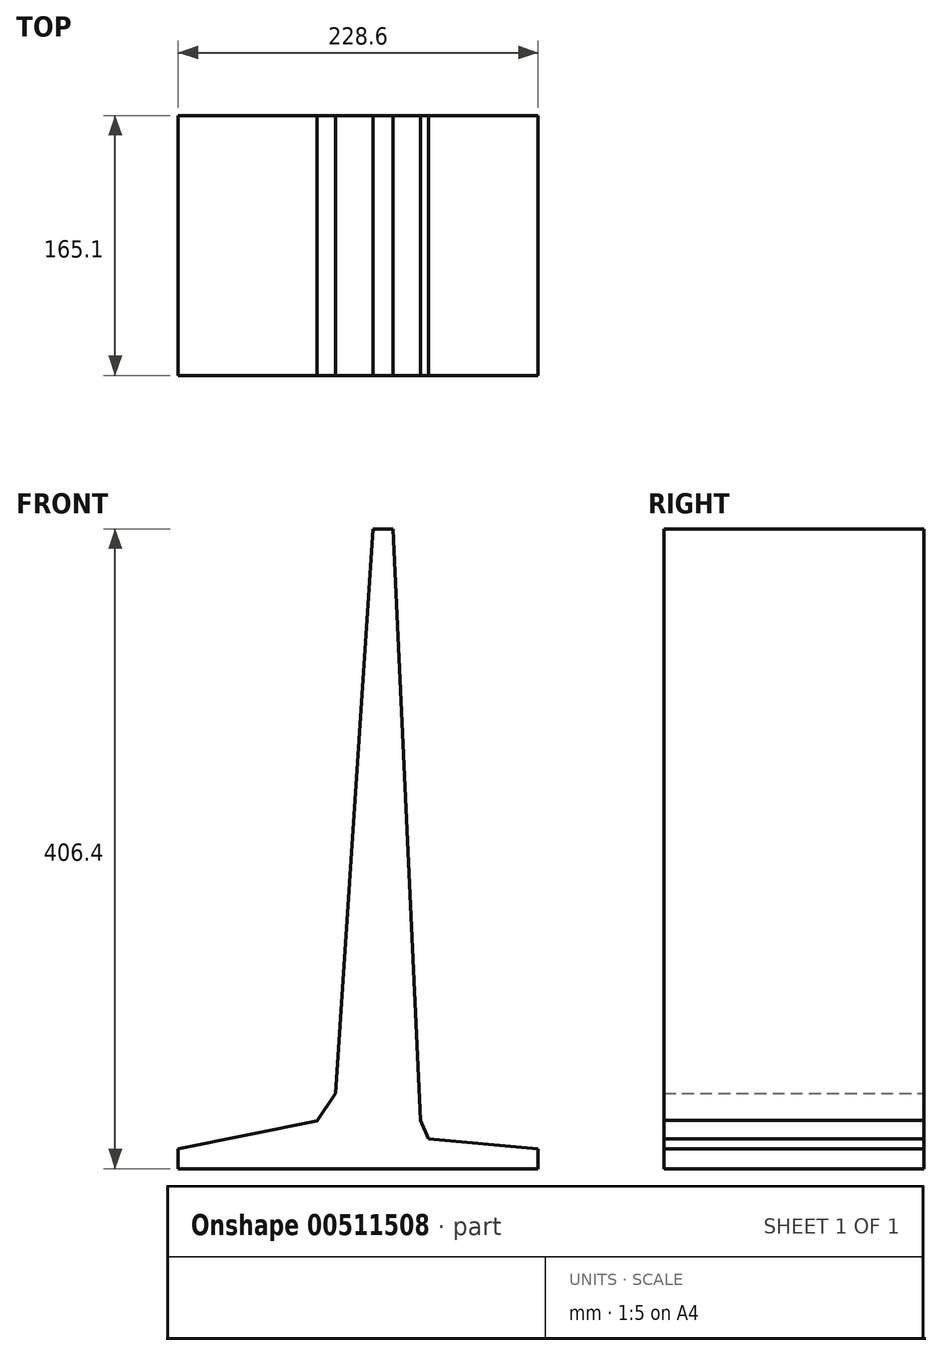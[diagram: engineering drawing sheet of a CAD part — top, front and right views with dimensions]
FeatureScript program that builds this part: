
annotation { "Feature Type Name" : "Feature", "Feature Type Description" : "" }
export const myFeature = defineFeature(function(context is Context, id is Id, definition is map)
    precondition{}
    {
        {
            var Q0;
            Q0=qCreatedBy(makeId("Front.planeOp"),FACE);
            var sketch = newSketch(context, id + "F0", { "sketchPlane" : qUnion([Q0])});
            skLineSegment(sketch, "E0", {"start": v(-130.16, 0) * mm, "end": v(98.44, 0) * mm});
            skLineSegment(sketch, "E1", {"start": v(98.44, 0) * mm, "end": v(98.44, 12.7) * mm});
            skLineSegment(sketch, "E2", {"start": v(98.44, 12.7) * mm, "end": v(28.7, 19.05) * mm});
            skLineSegment(sketch, "E3", {"start": v(28.7, 19.05) * mm, "end": v(23.86, 30.8) * mm});
            skLineSegment(sketch, "E4", {"start": v(23.86, 30.8) * mm, "end": v(6.35, 406.4) * mm});
            skLineSegment(sketch, "E5", {"start": v(6.35, 406.4) * mm, "end": v(-6.35, 406.4) * mm});
            skLineSegment(sketch, "E6", {"start": v(-6.35, 406.4) * mm, "end": v(-30.36, 47.9) * mm});
            skLineSegment(sketch, "E7", {"start": v(-30.36, 47.9) * mm, "end": v(-42.1, 30.43) * mm});
            skLineSegment(sketch, "E8", {"start": v(-42.1, 30.43) * mm, "end": v(-130.16, 12.7) * mm});
            skLineSegment(sketch, "E9", {"start": v(-130.16, 12.7) * mm, "end": v(-130.16, 0) * mm});
            skSolve(sketch);
        }
        {
            var Q0;
            Q0=makeQuery(id+"F0.imprint","IMPRINT",FACE,{"disambiguationData":[TD([[makeQuery(id+"F0.imprint","IMPRINT",EDGE,{"derivedFrom":sQuery(id+"F0.wireOp",EDGE,"E0")}),1.0]])]});
            extrude(context, id + "F1", {"entities" : qUnion([Q0]), "endBound" : BoundingType.SYMMETRIC, "depth" : 165.1 * mm});
        }
    });
